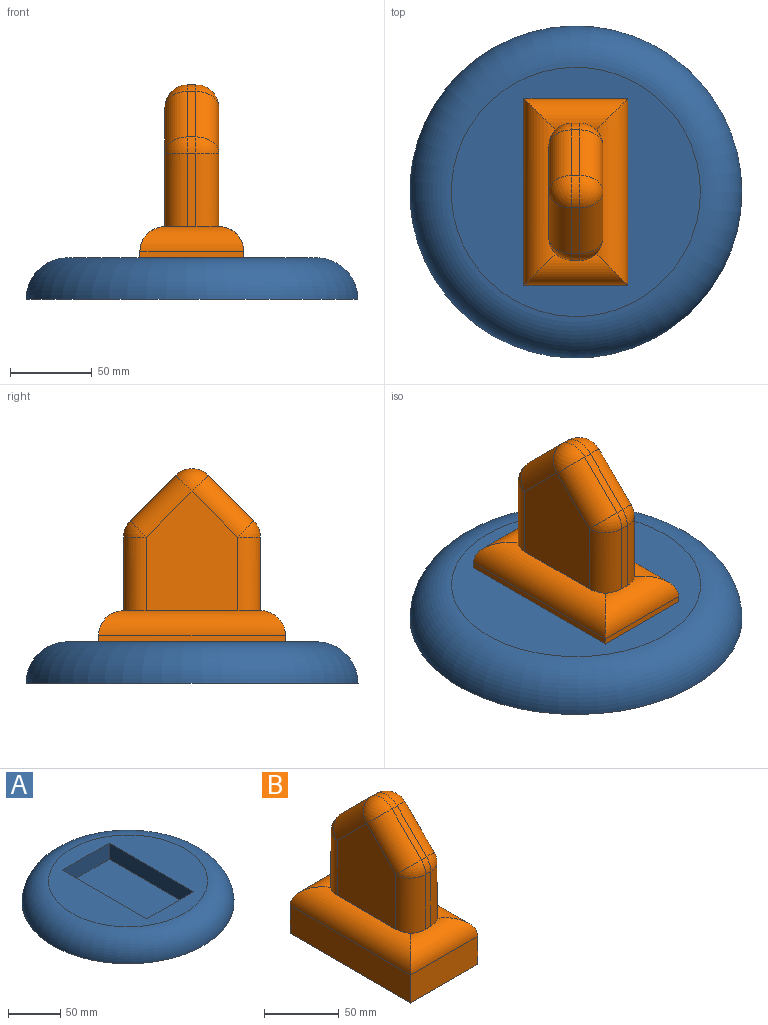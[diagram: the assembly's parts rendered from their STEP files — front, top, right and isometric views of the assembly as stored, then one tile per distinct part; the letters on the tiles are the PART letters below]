
ASSEMBLY  parts=2 mates=1
PART A: 8 faces, bbox 219.9x219.9x25.4 mm
  f0: plane 152.4x152.4mm, normal (0,0,1), area 10983.4mm2, adj f2,f3,f4,f5,f6
  f1: plane 203.2x203.2mm, normal (0,0,-1), area 32429.3mm2, adj f2
  f2: torus R=76.2mm, axis (0,0,1), area 23156.1mm2, adj f0,f1
  f3: plane 114.3x19.05mm, normal (-1,0,0), area 2177.4mm2, adj f0,f4,f6,f7
  f4: plane 63.5x19.05mm, normal (0,-1,0), area 1209.7mm2, adj f0,f3,f5,f7
  f5: plane 114.3x19.05mm, normal (1,0,0), area 2177.4mm2, adj f0,f4,f6,f7
  f6: plane 63.5x19.05mm, normal (0,1,0), area 1209.7mm2, adj f0,f3,f5,f7
  f7: plane 114.3x63.5mm, normal (0,0,1), area 7258.1mm2, adj f3,f4,f5,f6
PART B: 32 faces, bbox 63.5x114.3x125 mm
  f0: plane 114.3x22.86mm, normal (1,0,0), area 2612.9mm2, adj f1,f3,f4,f5
  f1: plane 63.5x22.86mm, normal (0,1,0), area 1451.6mm2, adj f0,f2,f4,f6
  f2: plane 114.3x22.86mm, normal (-1,0,0), area 2612.9mm2, adj f1,f3,f4,f8
  f3: plane 63.5x22.86mm, normal (0,-1,0), area 1451.6mm2, adj f0,f2,f4,f7
  f4: plane 114.3x63.5mm, normal (0,0,-1), area 7258.1mm2, adj f0,f1,f2,f3
  f5: cylinder r=15.24mm len=114.3mm, axis (0,-1,0), area 2513.7mm2, adj f0,f6,f7,f9,f15,f26
  f6: cylinder r=15.24mm len=63.5mm, axis (1,0,0), area 1297.6mm2, adj f1,f5,f8,f10,f15,f16
  f7: cylinder r=15.24mm len=63.5mm, axis (-1,0,0), area 1297.6mm2, adj f3,f5,f8,f12,f26,f27
  f8: cylinder r=15.24mm len=114.3mm, axis (0,1,0), area 2513.7mm2, adj f2,f6,f7,f11,f16,f27
  f9: plane 72.83x55.7mm, normal (1,0,0), area 3281.1mm2, adj f5,f15,f20,f25,f26
  f10: plane 44.98x4.9mm, normal (0,1,0), area 220.5mm2, adj f6,f15,f16,f17
  f11: plane 72.83x55.7mm, normal (-1,0,0), area 3281.1mm2, adj f8,f16,f21,f27,f28
  f12: plane 44.98x4.9mm, normal (0,-1,0), area 220.5mm2, adj f7,f26,f27,f31
  f13: plane 27.85x27.85mm, normal (0,-0.71,0.71), area 193.1mm2, adj f22,f25,f28,f31
  f14: plane 27.85x27.85mm, normal (0,0.71,0.71), area 193.1mm2, adj f17,f20,f21,f22
  f15: cylinder r=14.06mm len=45.54mm, axis (0,0,-1), area 995.8mm2, adj f5,f6,f9,f10,f18
  f16: cylinder r=14.06mm len=45.54mm, axis (0,0,-1), area 995.8mm2, adj f6,f8,f10,f11,f19
  f17: cylinder r=14.06mm len=9.94mm, axis (-1,0,0), area 54.1mm2, adj f10,f14,f18,f19
  f18: sphere r=14.06mm, area 155.2mm2, adj f15,f17,f20
  f19: sphere r=14.06mm, area 155.2mm2, adj f16,f17,f21
  f20: cylinder r=14.06mm len=37.79mm, axis (0,0.71,-0.71), area 869.8mm2, adj f9,f14,f18,f23
  f21: cylinder r=14.06mm len=37.79mm, axis (0,-0.71,0.71), area 869.8mm2, adj f11,f14,f19,f24
  f22: cylinder r=14.06mm len=19.88mm, axis (1,0,0), area 108.3mm2, adj f13,f14,f23,f24
  f23: sphere r=14.06mm, area 310.4mm2, adj f20,f22,f25
  f24: sphere r=14.06mm, area 310.4mm2, adj f21,f22,f28
  f25: cylinder r=14.06mm len=37.79mm, axis (0,0.71,0.71), area 869.8mm2, adj f9,f13,f23,f29
  f26: cylinder r=14.06mm len=45.54mm, axis (0,0,-1), area 995.8mm2, adj f5,f7,f9,f12,f29
  f27: cylinder r=14.06mm len=45.54mm, axis (0,0,-1), area 995.8mm2, adj f7,f8,f11,f12,f30
  f28: cylinder r=14.06mm len=37.79mm, axis (0,-0.71,-0.71), area 869.8mm2, adj f11,f13,f24,f30
  f29: sphere r=14.06mm, area 155.2mm2, adj f25,f26,f31
  f30: sphere r=14.06mm, area 155.2mm2, adj f27,f28,f31
  f31: cylinder r=14.06mm len=9.94mm, axis (1,0,0), area 54.1mm2, adj f12,f13,f29,f30
PLACE A at identity
PLACE B t=(0,0,6.35)mm
MATE fastened B.f1 <-> A.f4  axis (0,1,0) through (31.75,57.15,6.35)mm
